# Revit family: Storage-Teknion-C2HE_Double_Credenza_Elevated-R2021
name_source: partatom
category: Furniture
units: mm (PartAtom-declared; Revit-internal decimal feet)

## family parameters
Always vertical = Yes
Cut with Voids When Loaded = No
OmniClass Number = 23.40.20.00
OmniClass Title = General Furniture and Specialties
Room Calculation Point = No
Shared = Yes
Work Plane-Based = No

## types (4) — shared parameters
Assembly Code = E2020200
Available Depth = 20 & 24 Inch
Available Width = 60 & 72 Inch
Manufacturer = Teknion
Manufacturer Fax = 416.661.4586
Part Number = C2HE
Series = Chronicle
Sustainability Data = https://www.teknion.com
URL = www.teknion.com
Unit Weight URL = http://www.teknion.com
Warranty = http://www.teknion.com
zero-valued in all types: Default Elevation

## per-type parameters (varying)
| type | Depth | Depth - Left | Depth - Right | Description | Model | Width | Width - Left | Width - Right |
| 20" Depth, 60" Width | 20 " | 20 " | 20 " | Double Credenza, Elevated, 20" Depth, 60" Width | C2HE__2060_ | 60 " | 30 " | 30 " |
| 20" Depth, 72" Width | 20 " | 20 " | 20 " | Double Credenza, Elevated, 20" Depth, 72" Width | C2HE__2072_ | 72 " | 36 " | 36 " |
| 24" Depth, 72" Width | 24 " | 24 " | 24 " | Double Credenza, Elevated, 24" Depth, 72" Width | C2HE__2472_ | 72 " | 36 " | 36 " |
| 24" Depth, 60" Width | 24 " | 24 " | 24 " | Double Credenza, Elevated, 24" Depth, 60" Width | C2HE__2460_ | 60 " | 30 " | 30 " |

## geometry (parser evidence)
native form markers: Sweep x12
no freeform markers — native parametric forms only
